# Revit family: E_FF109 Downlighter Cover(300,350mm)
name_source: partatom
category: Specialty Equipment
revit_build: Autodesk Revit 2015 (Build: 20160512_0715(x64)
units: mm (PartAtom-declared; Revit-internal decimal feet)

## types (2) — shared parameters
Cut-Out Size = 145-270mm
IFC Classification = Building Element Proxy
Manufacturer = Tenmat ltd
Material/Grade = Firefly 109
Performance = BS EN 1366-3:2009 & BS 476, ETA-12/0332, 1224-CPR-0341, CE Marked
URL = https://www.tenmat.com
Wall Thickness = 14 mm  [stored 0.0459318 ft]

## per-type parameters (varying)
| type | Description | Height | Radius | Tenmat Item Number | Top Radius |
| 300mm | Firefly 109 300mm Downlighter Cover | 228 mm | 185 mm  [stored 0.606955 ft] | I109MC01200300017003 | 160 mm |
| 350mm | Firefly 109 350mm Downlighter Cover | 278 mm  [stored 0.912073 ft] | 215 mm | I109MC01200350023000 | 185 mm  [stored 0.606955 ft] |

note: [stored X ft] marks values corroborated as IEEE doubles in the binary element streams (Revit-internal decimal feet)

## geometry (parser evidence)
native form markers: Blend x2, Sweep x3
no freeform markers — native parametric forms only
